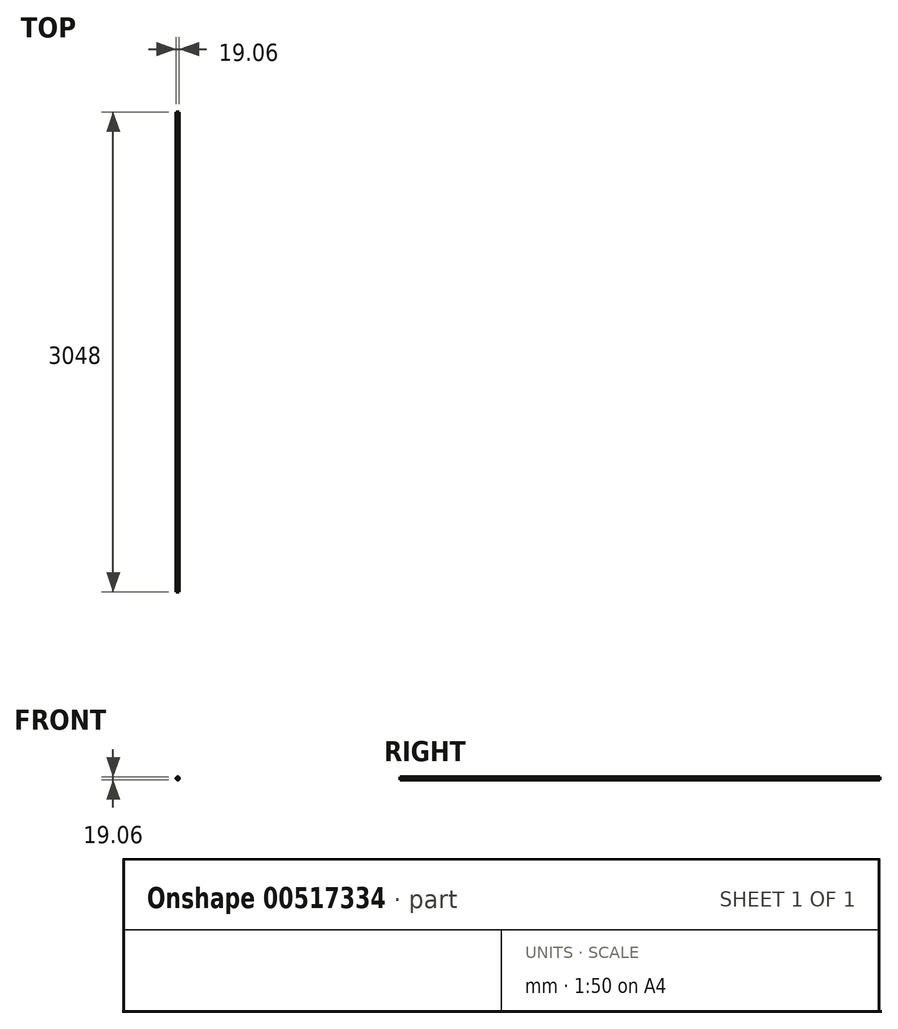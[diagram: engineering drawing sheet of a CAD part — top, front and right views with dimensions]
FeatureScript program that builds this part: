
annotation { "Feature Type Name" : "Feature", "Feature Type Description" : "" }
export const myFeature = defineFeature(function(context is Context, id is Id, definition is map)
    precondition{}
    {
        {
            var Q0;
            Q0=qCreatedBy(makeId("Front.planeOp"),FACE);
            var sketch = newSketch(context, id + "F0", { "sketchPlane" : qUnion([Q0])});
            skCircle(sketch, "E0", {"center": v(0, 0) * mm, "radius": 9.53 * mm});
            skSolve(sketch);
        }
        {
            var Q0;
            Q0=makeQuery(id+"F0.imprint","IMPRINT",FACE,{"disambiguationData":[TD([[makeQuery(id+"F0.imprint","IMPRINT",EDGE,{"derivedFrom":sQuery(id+"F0.wireOp",EDGE,"E0")}),1.0]])]});
            extrude(context, id + "F1", {"entities" : qUnion([Q0]), "oppositeDirection" : true, "depth" : 3048 * mm, "offsetDistance" : 25.4 * mm});
        }
    });
